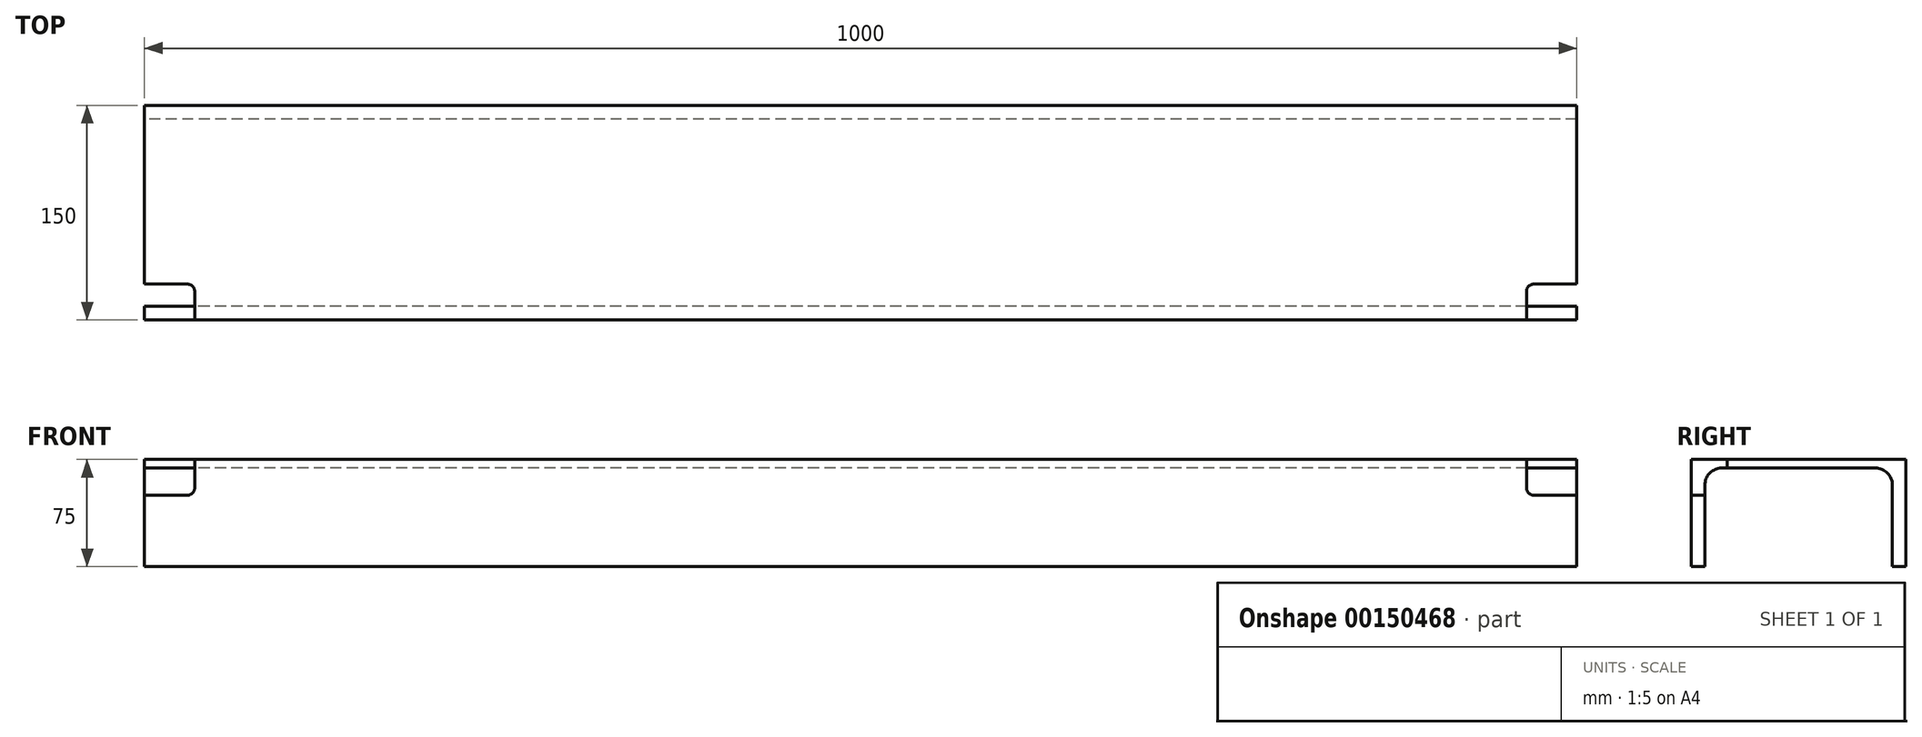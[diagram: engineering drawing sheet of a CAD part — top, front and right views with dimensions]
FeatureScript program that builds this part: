
annotation { "Feature Type Name" : "Feature", "Feature Type Description" : "" }
export const myFeature = defineFeature(function(context is Context, id is Id, definition is map)
    precondition{}
    {
        {
            var Q0;
            Q0=qCreatedBy(makeId("Right.planeOp"),FACE);
            var sketch = newSketch(context, id + "F0", { "sketchPlane" : qUnion([Q0])});
            skLineSegment(sketch, "E0", {"start": v(0, 0) * mm, "end": v(0, 75) * mm});
            skLineSegment(sketch, "E1", {"start": v(0, 75) * mm, "end": v(150, 75) * mm});
            skLineSegment(sketch, "E2", {"start": v(150, 75) * mm, "end": v(150, 0) * mm});
            skLineSegment(sketch, "E3", {"start": v(150, 0) * mm, "end": v(140.5, 0) * mm});
            skLineSegment(sketch, "E4", {"start": v(140.5, 0) * mm, "end": v(140.5, 57) * mm});
            skLineSegment(sketch, "E5", {"start": v(128.5, 69) * mm, "end": v(21.5, 69) * mm});
            skLineSegment(sketch, "E6", {"start": v(9.5, 57) * mm, "end": v(9.5, 0) * mm});
            skLineSegment(sketch, "E7", {"start": v(9.5, 0) * mm, "end": v(0, 0) * mm});
            skPoint(sketch, "E8.visualSharp", {"position": v(9.5, 69) * mm});
            skArc(sketch, "E8.filletArc", {"start": v(21.5, 69) * mm, "mid": v(13.01, 65.49) * mm, "end": v(9.5, 57) * mm});
            skPoint(sketch, "E9.visualSharp", {"position": v(140.5, 69) * mm});
            skArc(sketch, "E9.filletArc", {"start": v(140.5, 57) * mm, "mid": v(136.99, 65.49) * mm, "end": v(128.5, 69) * mm});
            skSolve(sketch);
        }
        {
            var Q0;
            Q0=makeQuery(id+"F0.imprint","IMPRINT",FACE,{"disambiguationData":[TD([[makeQuery(id+"F0.imprint","IMPRINT",EDGE,{"derivedFrom":sQuery(id+"F0.wireOp",EDGE,"E0")}),-1.0]])]});
            extrude(context, id + "F1", {"entities" : qUnion([Q0]), "depth" : 500 * mm});
        }
        {
            var Q0;
            Q0=qCreatedBy(makeId("Front.planeOp"),FACE);
            var sketch = newSketch(context, id + "F2", { "sketchPlane" : qUnion([Q0])});
            skLineSegment(sketch, "E10.bottom", {"start": v(500, 75) * mm, "end": v(465, 75) * mm});
            skLineSegment(sketch, "E10.top", {"start": v(500, 50) * mm, "end": v(465, 50) * mm});
            skLineSegment(sketch, "E10.left", {"start": v(500, 75) * mm, "end": v(500, 50) * mm});
            skLineSegment(sketch, "E10.right", {"start": v(465, 75) * mm, "end": v(465, 50) * mm});
            skSolve(sketch);
        }
        {
            var Q0;
            Q0=makeQuery(id+"F2.imprint","IMPRINT",FACE,{"disambiguationData":[TD([[makeQuery(id+"F2.imprint","IMPRINT",EDGE,{"derivedFrom":sQuery(id+"F2.wireOp",EDGE,"E10.bottom")}),1.0]])]});
            extrude(context, id + "F3", {"entities" : qUnion([Q0]), "operationType" : NewBodyOperationType.REMOVE, "oppositeDirection" : true, "depth" : 25 * mm});
        }
        {
            var Q0;
            Q0=makeQuery(id+"F3.boolean.opBoolean","COPY",EDGE,{"derivedFrom":makeQuery(id+"F3.opExtrude","CAP_EDGE",EDGE,{"disambiguationData":[OSD([sQuery(id+"F2.wireOp",EDGE,"E10.right")])],"isStart":false})});
            var Q1;
            Q1=makeQuery(id+"F3.boolean.opBoolean","COPY",EDGE,{"derivedFrom":makeQuery(id+"F3.opExtrude","SWEPT_EDGE",EDGE,{"disambiguationData":[OSD([sQuery(id+"F2.wireOp",EDGE,"E10.top"),sQuery(id+"F2.wireOp",EDGE,"E10.right")])]})});
            fillet(context, id + "F4", {"entities" : qUnion([Q0, Q1]), "radius" : 5 * mm, "tangentPropagation" : true, "allowEdgeOverflow" : false});
        }
        {
            var Q0;
            Q0=makeQuery(id+"F1.opExtrude","SWEPT_BODY",BODY,{"disambiguationData":[OSD([sQuery(id+"F0.wireOp",EDGE,"E0"),sQuery(id+"F0.wireOp",EDGE,"E1"),sQuery(id+"F0.wireOp",EDGE,"E2"),sQuery(id+"F0.wireOp",EDGE,"E3"),sQuery(id+"F0.wireOp",EDGE,"E4"),sQuery(id+"F0.wireOp",EDGE,"E5"),sQuery(id+"F0.wireOp",EDGE,"E6"),sQuery(id+"F0.wireOp",EDGE,"E7"),sQuery(id+"F0.wireOp",EDGE,"E8.filletArc"),sQuery(id+"F0.wireOp",EDGE,"E9.filletArc")])]});
            var Q1;
            Q1=qCreatedBy(makeId("Right.planeOp"),FACE);
            mirror(context, id + "F5", {"operationType" : NewBodyOperationType.ADD, "entities" : qUnion([Q0]), "mirrorPlane" : qUnion([Q1])});
        }
    });
